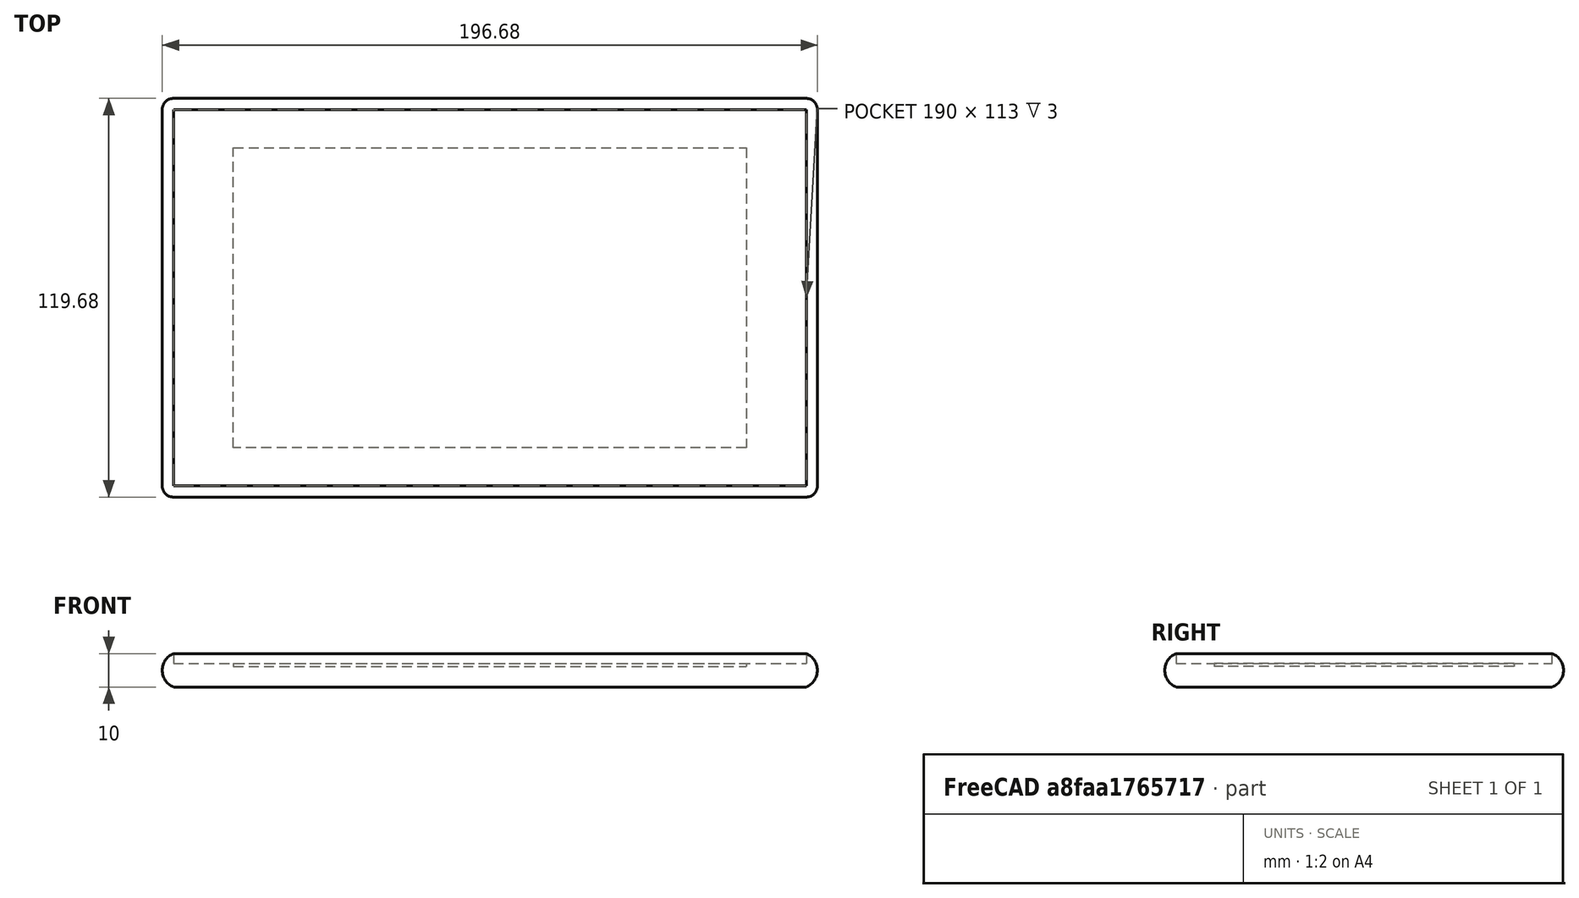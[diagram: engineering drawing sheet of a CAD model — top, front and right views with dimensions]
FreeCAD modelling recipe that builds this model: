
FCSTD DOCUMENT  (FreeCAD 0.19R24344 (Git))
Label: FireTablet
Comment: Rough sketch of the Amazon Fire tablet.
License: Creative Commons Attribution-NonCommercial-ShareAlike
LicenseURL: http://creativecommons.org/licenses/by-nc-sa/4.0/
objects: Sketcher::SketchObject×9, PartDesign::Pad×5, PartDesign::Revolution×4, PartDesign::Body×3, PartDesign::CoordinateSystem×2, App::Part×1
note: 32 computed .brp shape members not serialized (recipe doc carries the construction recipe); baked Part::Feature solids carry a one-line shape summary decoded from their .brp

FEATURE [Sketcher::SketchObject] Sketch
  FullyConstrained = true
  MapMode = 5
  Support = -> [XY_Plane]
  sketch-geometry (4):
    g0: LineSegment StartX=-95 StartY=56.5 StartZ=0 EndX=95 EndY=56.5 EndZ=0
    g1: LineSegment StartX=95 StartY=56.5 StartZ=0 EndX=95 EndY=-56.5 EndZ=0
    g2: LineSegment StartX=95 StartY=-56.5 StartZ=0 EndX=-95 EndY=-56.5 EndZ=0
    g3: LineSegment StartX=-95 StartY=-56.5 StartZ=0 EndX=-95 EndY=56.5 EndZ=0
  constraints (10):
    c: Coincident(g0,g1)
    c: Coincident(g1,g2)
    c: Coincident(g2,g3)
    c: Coincident(g3,g0)
    c: Horizontal(g2)
    c: Vertical(g1)
    c: DistanceX(g0,g0) = 190
    c: DistanceY(g3,g3) = 113
    c: Symmetric(g0,g0,g-2)
    c: Symmetric(g0,g2,g-1)
FEATURE [PartDesign::Pad] Pad
  Direction = (1,1,1)
  Length = 3
  Length2 = 100
  Profile = -> Sketch
  Type = 0
FEATURE [PartDesign::Body] Body  label="Front Glass"
  Group = -> [Sketch,Pad]
  Origin = -> Origin
  Tip = -> Pad
FEATURE [Sketcher::SketchObject] Sketch001
  FullyConstrained = true
  MapMode = 5
  Placement = pos=(0,0,0) rot=(0.57735,0.57735,0.57735;2.0944rad)
  Support = -> [YZ_Plane001]
  sketch-geometry (6):
    g0: ArcOfCircle CenterX=-54.4289 CenterY=-2 CenterZ=0 NormalX=0 NormalY=0 NormalZ=1 AngleXU=0 Radius=5.41196 StartAngle=1.9635 EndAngle=4.31969
    g1: ArcOfCircle CenterX=54.4289 CenterY=-2 CenterZ=0 NormalX=0 NormalY=0 NormalZ=1 AngleXU=0 Radius=5.41196 StartAngle=5.10509 EndAngle=7.46128
    g2: LineSegment StartX=-56.5 StartY=-7 StartZ=0 EndX=56.5 EndY=-7 EndZ=0
    g3: LineSegment StartX=-56.5 StartY=3 StartZ=0 EndX=-56.5 EndY=0 EndZ=0
    g4: LineSegment StartX=-56.5 StartY=0 StartZ=0 EndX=56.5 EndY=0 EndZ=0
    g5: LineSegment StartX=56.5 StartY=0 StartZ=0 EndX=56.5 EndY=3 EndZ=0
  constraints (19):
    c: DistanceY(g0,g0) = 10
    c: DistanceY(g1,g1) = 10
    c: Vertical(g0,g0)
    c: Vertical(g1,g1)
    c: DistanceX(g0,g-1) = 56.5
    c: DistanceY(g-1,g0) = 3
    c: Symmetric(g0,g1,g-2)
    c: Angle(g0) = 2.35619
    c: Angle(g1) = 2.35619
    c: Coincident(g2,g0)
    c: Coincident(g2,g1)
    c: Coincident(g3,g0)
    c: PointOnObject(g3,g-1)
    c: Vertical(g3)
    c: Coincident(g4,g3)
    c: PointOnObject(g4,g-1)
    c: Coincident(g5,g4)
    c: Coincident(g5,g1)
    c: Vertical(g5)
FEATURE [PartDesign::Pad] Pad001
  Direction = (1,1,1)
  Length = 190
  Length2 = 100
  Midplane = true
  Placement = pos=(0,0,0) rot=(0.57735,0.57735,0.57735;2.0944rad)
  Profile = -> Sketch001
  Type = 0
FEATURE [Sketcher::SketchObject] Sketch002
  ExternalGeometry = -> [Pad001]
  FullyConstrained = true
  MapMode = 5
  Placement = pos=(0,0,0) rot=(1,0,0;1.5708rad)
  Support = -> [XZ_Plane001]
  sketch-geometry (2):
    g0: ArcOfCircle CenterX=-92.9289 CenterY=-2 CenterZ=0 NormalX=0 NormalY=0 NormalZ=1 AngleXU=0 Radius=5.41196 StartAngle=1.9635 EndAngle=4.31969
    g1: LineSegment StartX=-95 StartY=3 StartZ=0 EndX=-95 EndY=-7 EndZ=0
  constraints (5):
    c: Coincident(g0,g-3)
    c: Coincident(g0,g-3)
    c: Angle(g0) = 2.35619
    c: Coincident(g1,g0)
    c: Coincident(g1,g0)
FEATURE [PartDesign::Pad] Pad002
  BaseFeature = -> Pad001
  Direction = (1,1,1)
  Length = 113
  Length2 = 100
  Midplane = true
  Placement = pos=(0,0,0) rot=(0.57735,0.57735,0.57735;2.0944rad)
  Profile = -> Sketch002
  Type = 0
FEATURE [Sketcher::SketchObject] Sketch003
  ExternalGeometry = -> [Pad002]
  FullyConstrained = true
  MapMode = 5
  Placement = pos=(0,0,0) rot=(1,0,0;1.5708rad)
  Support = -> [XZ_Plane001]
  sketch-geometry (2):
    g0: ArcOfCircle CenterX=92.9289 CenterY=-2 CenterZ=0 NormalX=0 NormalY=0 NormalZ=1 AngleXU=0 Radius=5.41196 StartAngle=5.10509 EndAngle=7.46128
    g1: LineSegment StartX=95 StartY=3 StartZ=0 EndX=95 EndY=-7 EndZ=0
  constraints (5):
    c: Coincident(g0,g-3)
    c: Coincident(g0,g-3)
    c: Coincident(g1,g0)
    c: Coincident(g1,g0)
    c: Angle(g0) = 2.35619
FEATURE [PartDesign::Pad] Pad003
  BaseFeature = -> Pad002
  Direction = (1,1,1)
  Length = 113
  Length2 = 100
  Midplane = true
  Placement = pos=(0,0,0) rot=(0.57735,0.57735,0.57735;2.0944rad)
  Profile = -> Sketch003
  Type = 0
FEATURE [Sketcher::SketchObject] Sketch005
  ExternalGeometry = -> [Pad003]
  FullyConstrained = true
  MapMode = 5
  Placement = pos=(0,-56.5,1.24e-14) rot=(0.57735,0.57735,-0.57735;2.0944rad)
  Support = -> [Pad003]
  sketch-geometry (2):
    g0: ArcOfCircle CenterX=2 CenterY=-92.9289 CenterZ=0 NormalX=0 NormalY=0 NormalZ=1 AngleXU=0 Radius=5.41196 StartAngle=3.53429 EndAngle=5.89049
    g1: LineSegment StartX=-3 StartY=-95 StartZ=0 EndX=7 EndY=-95 EndZ=0
  constraints (5):
    c: Coincident(g0,g-3)
    c: Coincident(g0,g-3)
    c: Tangent(g0,g-3)
    c: Coincident(g1,g0)
    c: Coincident(g1,g0)
FEATURE [PartDesign::Revolution] Revolution
  Angle = 90
  Axis = (7e-16,-4e-16,-1)
  Base = (-95,-56.5,3)
  BaseFeature = -> Pad003
  Placement = pos=(0,0,0) rot=(0.57735,0.57735,0.57735;2.0944rad)
  Profile = -> Sketch005
  ReferenceAxis = -> Pad003 [Edge11]
  Reversed = true
FEATURE [Sketcher::SketchObject] Sketch006
  ExternalGeometry = -> [Revolution]
  FullyConstrained = true
  MapMode = 5
  Placement = pos=(-95,2.09e-14,-2.09e-14) rot=(0.57735,0.57735,-0.57735;4.18879rad)
  Support = -> [Revolution]
  sketch-geometry (2):
    g0: ArcOfCircle CenterX=54.4289 CenterY=2 CenterZ=0 NormalX=0 NormalY=0 NormalZ=1 AngleXU=0 Radius=5.41196 StartAngle=5.10509 EndAngle=7.46128
    g1: LineSegment StartX=56.5 StartY=7 StartZ=0 EndX=56.5 EndY=-3 EndZ=0
  constraints (5):
    c: Coincident(g0,g-3)
    c: Coincident(g0,g-3)
    c: Coincident(g0,g1)
    c: Coincident(g1,g0)
    c: Angle(g0) = 2.35619
FEATURE [PartDesign::Revolution] Revolution001
  Angle = 90
  Axis = (1e-15,-6e-16,-1)
  Base = (-95,56.5,3)
  BaseFeature = -> Revolution
  Placement = pos=(0,0,0) rot=(0.57735,0.57735,0.57735;2.0944rad)
  Profile = -> Sketch006
  ReferenceAxis = -> Revolution [Edge28]
  Reversed = true
FEATURE [Sketcher::SketchObject] Sketch007
  ExternalGeometry = -> [Revolution001]
  FullyConstrained = true
  MapMode = 5
  Placement = pos=(95,-2.09e-14,2.09e-14) rot=(0.57735,0.57735,0.57735;2.0944rad)
  Support = -> [Revolution001]
  sketch-geometry (2):
    g0: ArcOfCircle CenterX=54.4289 CenterY=-2 CenterZ=0 NormalX=0 NormalY=0 NormalZ=1 AngleXU=0 Radius=5.41196 StartAngle=5.10509 EndAngle=7.46128
    g1: LineSegment StartX=56.5 StartY=3 StartZ=0 EndX=56.5 EndY=-7 EndZ=0
  constraints (5):
    c: Coincident(g0,g-3)
    c: Coincident(g0,g-3)
    c: Tangent(g0,g-3)
    c: Coincident(g1,g0)
    c: Coincident(g1,g0)
FEATURE [PartDesign::Revolution] Revolution002
  Angle = 90
  Axis = (3.8e-15,-6e-16,-1)
  Base = (95,56.5,3)
  BaseFeature = -> Revolution001
  Placement = pos=(0,0,0) rot=(0.57735,0.57735,0.57735;2.0944rad)
  Profile = -> Sketch007
  ReferenceAxis = -> Revolution001 [Edge30]
FEATURE [Sketcher::SketchObject] Sketch008
  ExternalGeometry = -> [Revolution002]
  FullyConstrained = true
  MapMode = 5
  Placement = pos=(95,-2.09e-14,2.09e-14) rot=(0.57735,0.57735,0.57735;2.0944rad)
  Support = -> [Revolution002]
  sketch-geometry (2):
    g0: ArcOfCircle CenterX=-54.4289 CenterY=-2 CenterZ=0 NormalX=0 NormalY=0 NormalZ=1 AngleXU=0 Radius=5.41196 StartAngle=1.9635 EndAngle=4.31969
    g1: LineSegment StartX=-56.5 StartY=3 StartZ=0 EndX=-56.5 EndY=-7 EndZ=0
  constraints (5):
    c: Coincident(g0,g-3)
    c: Coincident(g0,g-3)
    c: Tangent(g0,g-3)
    c: Coincident(g1,g0)
    c: Coincident(g1,g0)
FEATURE [PartDesign::Revolution] Revolution003
  Angle = 90
  Axis = (4.2e-15,-7e-16,-1)
  Base = (95,-56.5,3)
  BaseFeature = -> Revolution002
  Placement = pos=(0,0,0) rot=(0.57735,0.57735,0.57735;2.0944rad)
  Profile = -> Sketch008
  ReferenceAxis = -> Revolution002 [Edge14]
  Reversed = true
FEATURE [PartDesign::Body] Body001  label="Case"
  Group = -> [Sketch001,Pad001,Sketch002,Pad002,Sketch003,Pad003,Sketch005,Revolution,Sketch006,Revolution001,Sketch007,Revolution002,Sketch008,Revolution003]
  Origin = -> Origin001
  Tip = -> Revolution003
FEATURE [Sketcher::SketchObject] Sketch009
  FullyConstrained = true
  MapMode = 5
  Support = -> [XY_Plane002]
  sketch-geometry (4):
    g0: LineSegment StartX=-77 StartY=45 StartZ=0 EndX=77 EndY=45 EndZ=0
    g1: LineSegment StartX=77 StartY=45 StartZ=0 EndX=77 EndY=-45 EndZ=0
    g2: LineSegment StartX=77 StartY=-45 StartZ=0 EndX=-77 EndY=-45 EndZ=0
    g3: LineSegment StartX=-77 StartY=-45 StartZ=0 EndX=-77 EndY=45 EndZ=0
  constraints (10):
    c: Coincident(g0,g1)
    c: Coincident(g1,g2)
    c: Coincident(g2,g3)
    c: Coincident(g3,g0)
    c: Horizontal(g2)
    c: Vertical(g1)
    c: DistanceX(g0,g0) = 154
    c: DistanceY(g3,g3) = 90
    c: Symmetric(g0,g0,g-2)
    c: Symmetric(g0,g2,g-1)
FEATURE [PartDesign::Pad] Pad004
  Direction = (1,1,1)
  Length = 1
  Length2 = 100
  Profile = -> Sketch009
  Reversed = true
  Type = 0
FEATURE [PartDesign::Body] Body002  label="Screen"
  Group = -> [Sketch009,Pad004]
  Origin = -> Origin002
  Placement = pos=(0,0,0.1) rot=(0,0,1;0rad)
  Tip = -> Pad004
FEATURE [PartDesign::CoordinateSystem] LCS_0
  AttacherType = Attacher::AttachEngine3D
  MapMode = 2
  Support = -> [X_Axis003]
FEATURE [PartDesign::CoordinateSystem] LCS_Tablet_Back
  AttacherType = Attacher::AttachEngine3D
  MapMode = 45
  Placement = pos=(6.5e-15,3e-16,-7) rot=(0,0,1;1.5708rad)
  Support = -> [Revolution003]
FEATURE [App::Part] Fire7
  Group = -> [LCS_0,Body,Body001,Body002,LCS_Tablet_Back]
  Origin = -> Origin003
